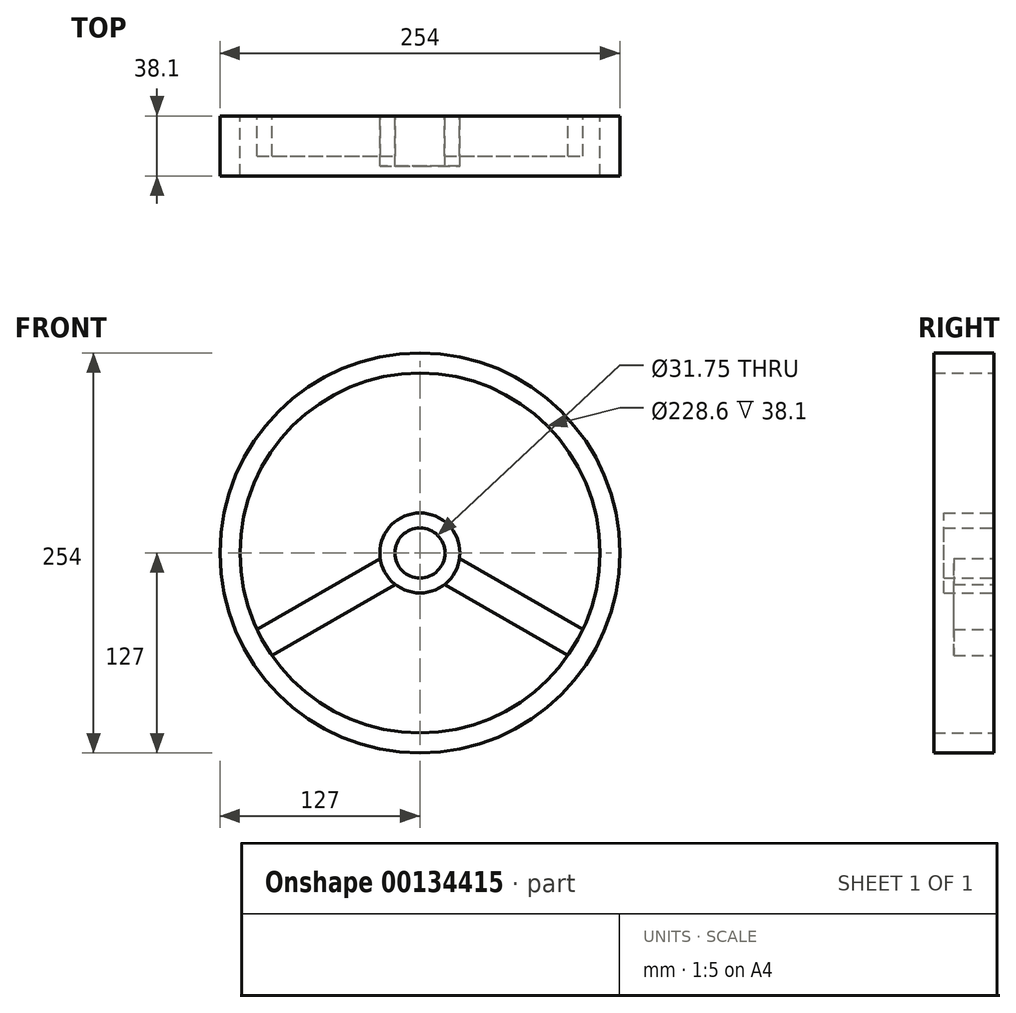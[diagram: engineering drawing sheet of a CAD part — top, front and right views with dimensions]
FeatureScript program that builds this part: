
annotation { "Feature Type Name" : "Feature", "Feature Type Description" : "" }
export const myFeature = defineFeature(function(context is Context, id is Id, definition is map)
    precondition{}
    {
        {
            var Q0;
            Q0=qCreatedBy(makeId("Front.planeOp"),FACE);
            var sketch = newSketch(context, id + "F0", { "sketchPlane" : qUnion([Q0])});
            skCircle(sketch, "E0", {"center": v(0, 0) * mm, "radius": 114.3 * mm});
            skCircle(sketch, "E1", {"center": v(0, 0) * mm, "radius": 127 * mm});
            skCircle(sketch, "E2", {"center": v(0, 0) * mm, "radius": 25.4 * mm});
            skCircle(sketch, "E3", {"center": v(0, 0) * mm, "radius": 15.88 * mm});
            skLineSegment(sketch, "E4", {"start": v(-103.4, -48.7) * mm, "end": v(-25.15, -3.52) * mm});
            skLineSegment(sketch, "E5", {"start": v(-93.88, -65.2) * mm, "end": v(-15.63, -20.02) * mm});
            skLineSegment(sketch, "E6", {"start": v(9.52, 113.9) * mm, "end": v(9.52, 23.55) * mm});
            skLineSegment(sketch, "E7", {"start": v(15.63, -20.02) * mm, "end": v(93.88, -65.2) * mm});
            skLineSegment(sketch, "E8", {"start": v(25.15, -3.52) * mm, "end": v(103.4, -48.7) * mm});
            skLineSegment(sketch, "E9", {"start": v(-9.53, 113.9) * mm, "end": v(-9.53, 23.55) * mm});
            skSolve(sketch);
        }
        {
            var Q0;
            Q0=makeQuery(id+"F0.imprint","IMPRINT",FACE,{"disambiguationData":[TD([[makeQuery(id+"F0.imprint","IMPRINT",EDGE,{"derivedFrom":sQuery(id+"F0.wireOp",EDGE,"E1")}),1.0]])]});
            extrude(context, id + "F1", {"entities" : qUnion([Q0]), "depth" : 38.1 * mm});
        }
        {
            var Q0;
            Q0=makeQuery(id+"F0.imprint","IMPRINT",FACE,{"disambiguationData":[TD([[makeQuery(id+"F0.imprint","IMPRINT",EDGE,{"derivedFrom":sQuery(id+"F0.wireOp",EDGE,"E3")}),-1.0]])]});
            extrude(context, id + "F2", {"entities" : qUnion([Q0]), "depth" : 31.75 * mm});
        }
        {
            var Q0;
            {var subQ0=sQuery(id+"F0.wireOp",EDGE,"E6");Q0=makeQuery(id+"F0.imprint","IMPRINT",FACE,{"disambiguationData":[TD([[makeQuery(id+"F0.imprint","IMPRINT",EDGE,{"derivedFrom":subQ0}),-1.0]])]});}
            var Q1;
            {var subQ0=sQuery(id+"F0.wireOp",EDGE,"E4");Q1=makeQuery(id+"F0.imprint","IMPRINT",FACE,{"disambiguationData":[TD([[makeQuery(id+"F0.imprint","IMPRINT",EDGE,{"derivedFrom":subQ0}),-1.0]])]});}
            var Q2;
            {var subQ0=sQuery(id+"F0.wireOp",EDGE,"E7");Q2=makeQuery(id+"F0.imprint","IMPRINT",FACE,{"disambiguationData":[TD([[makeQuery(id+"F0.imprint","IMPRINT",EDGE,{"derivedFrom":subQ0}),1.0]])]});}
            extrude(context, id + "F3", {"entities" : qUnion([Q0, Q1, Q2]), "depth" : 25.4 * mm});
        }
    });
